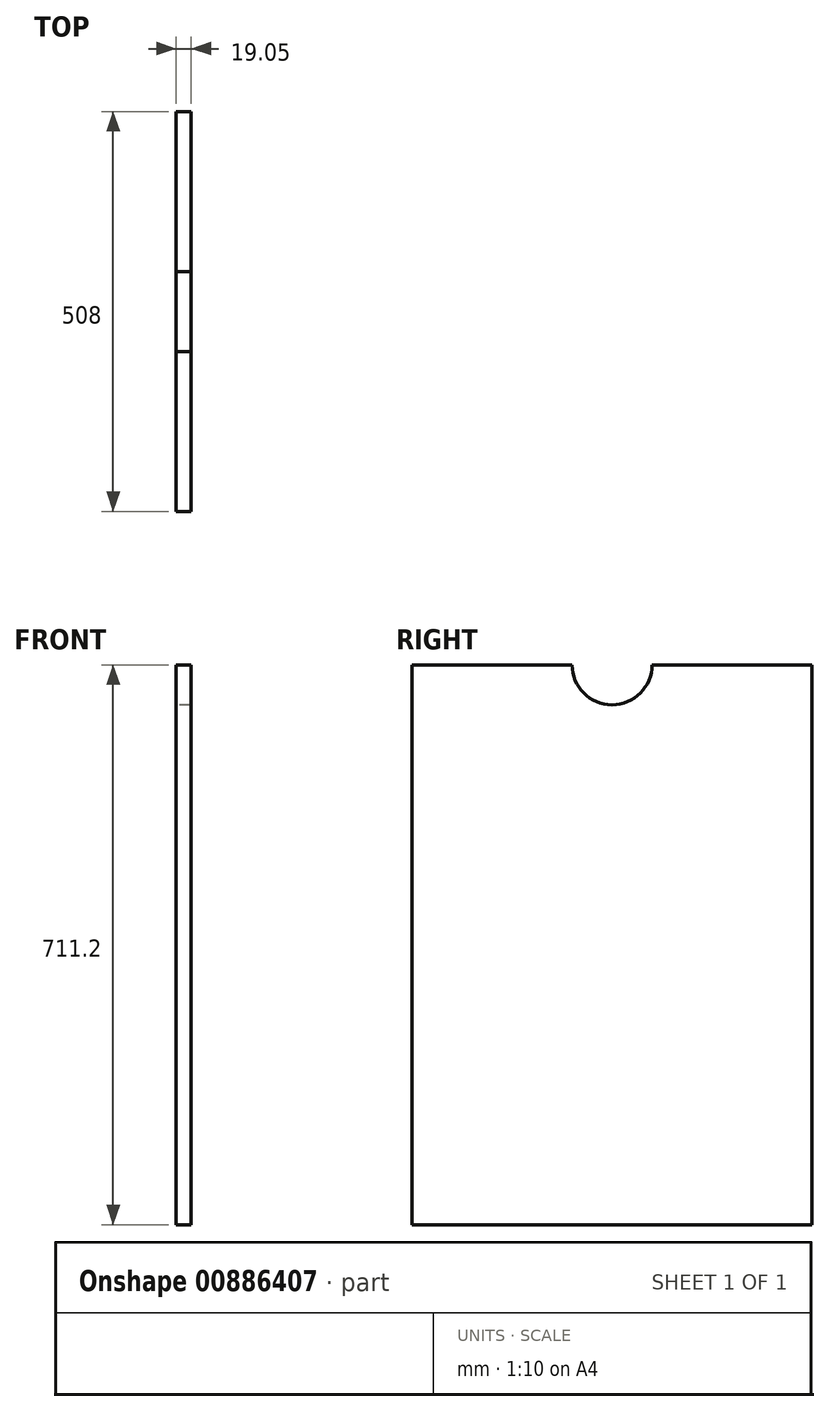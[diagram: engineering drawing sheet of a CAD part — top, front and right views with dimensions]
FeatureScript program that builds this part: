
annotation { "Feature Type Name" : "Feature", "Feature Type Description" : "" }
export const myFeature = defineFeature(function(context is Context, id is Id, definition is map)
    precondition{}
    {
        {
            var Q0;
            Q0=qCreatedBy(makeId("Right.planeOp"),FACE);
            var sketch = newSketch(context, id + "F0", { "sketchPlane" : qUnion([Q0])});
            skLineSegment(sketch, "E0.bottom", {"start": v(254, 355.6) * mm, "end": v(-254, 355.6) * mm});
            skLineSegment(sketch, "E0.top", {"start": v(254, -355.6) * mm, "end": v(-254, -355.6) * mm});
            skLineSegment(sketch, "E0.left", {"start": v(254, 355.6) * mm, "end": v(254, -355.6) * mm});
            skLineSegment(sketch, "E0.right", {"start": v(-254, 355.6) * mm, "end": v(-254, -355.6) * mm});
            skPoint(sketch, "E0.middle", {"position": v(0, 0) * mm});
            skCircle(sketch, "E1", {"center": v(0, 355.6) * mm, "radius": 50.8 * mm});
            skSolve(sketch);
        }
        {
            var Q0;
            Q0=makeQuery(id+"F0.imprint","IMPRINT",FACE,{"disambiguationData":[TD([[makeQuery(id+"F0.imprint","IMPRINT",EDGE,{"derivedFrom":sQuery(id+"F0.wireOp",EDGE,"E0.top")}),-1.0]])]});
            extrude(context, id + "F1", {"entities" : qUnion([Q0]), "depth" : 19.05 * mm, "offsetDistance" : 25.4 * mm});
        }
    });
